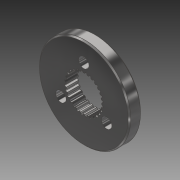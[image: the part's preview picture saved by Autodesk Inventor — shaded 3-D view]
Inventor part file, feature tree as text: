
AUTODESK INVENTOR PART (.ipt)
format: ipt  version: 2014 SP1 (Build 180222100, 222)  size: 323,584 bytes
history: native  units: in
note: dims shown in document units (in); Inventor stores cm internally (conversion verified against a paired STEP export)
features: chamfer x1, other x1, imported_body x1
ambient origin geometry x8: Origin, YZ Plane, XZ Plane, XY Plane, X Axis, Y Axis, Z Axis, Center Point
bodies: Body1 (feature_tree)
feature tree (3):
  chamfer  "Chamfer1"  [1 undecoded]
  other  "217-2625-008 Rev1.ipt1"
  imported_body  "Base1"
note: 1 required parameter value undecoded (feature->parameter linkage not recoverable at this tier; creation-order binding heuristic only, values carry confidence <= 0.55)
